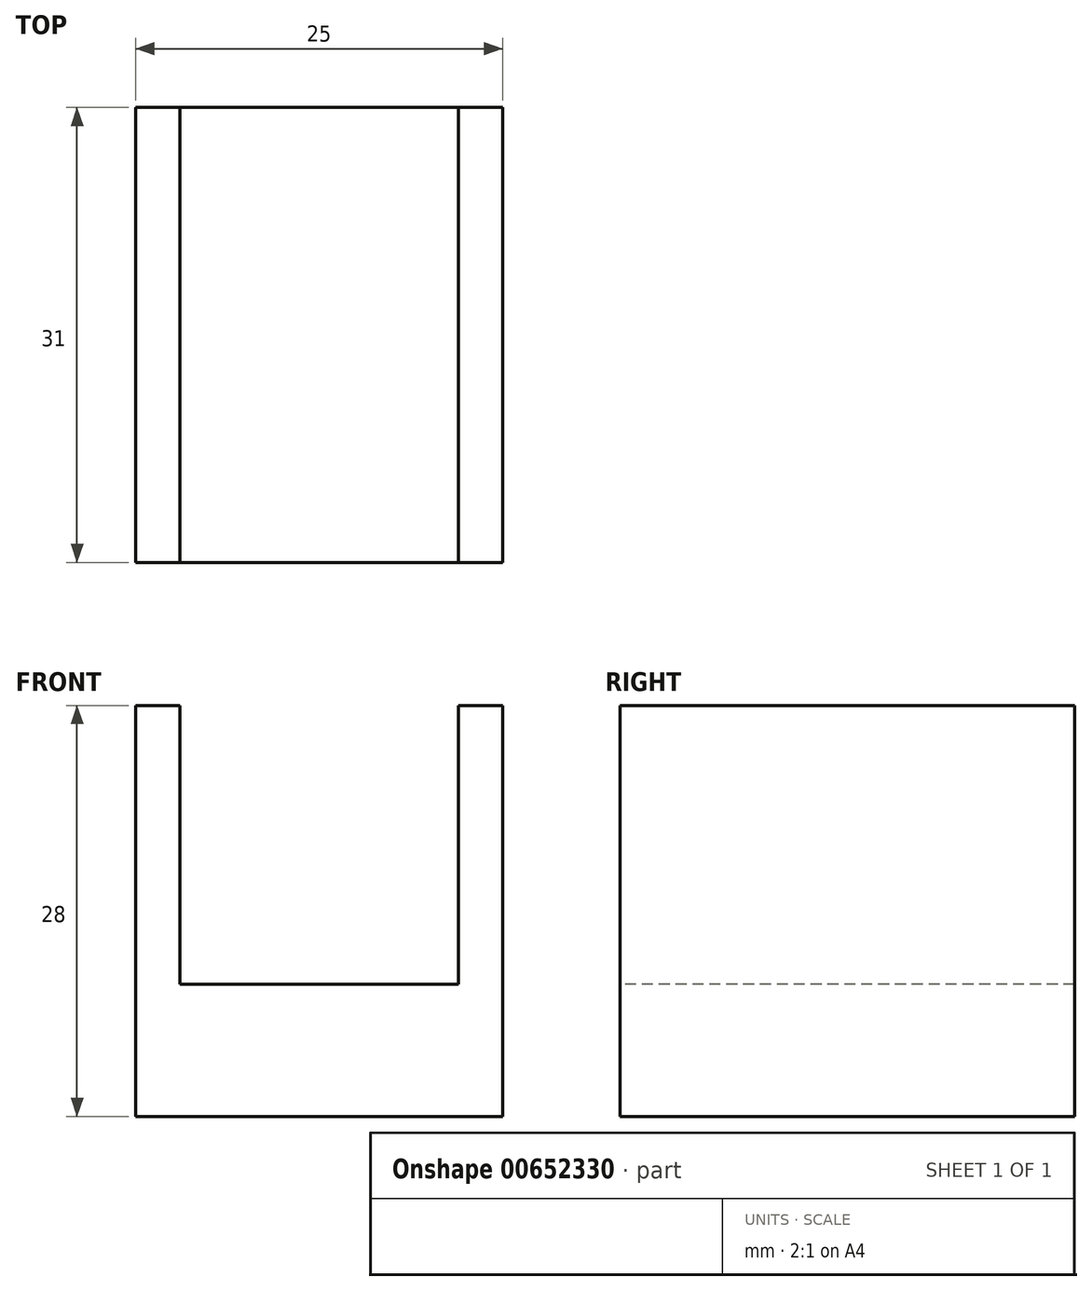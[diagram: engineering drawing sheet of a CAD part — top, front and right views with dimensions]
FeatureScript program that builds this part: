
annotation { "Feature Type Name" : "Feature", "Feature Type Description" : "" }
export const myFeature = defineFeature(function(context is Context, id is Id, definition is map)
    precondition{}
    {
        {
            var Q0;
            Q0=qCreatedBy(makeId("Top.planeOp"),FACE);
            var sketch = newSketch(context, id + "F0", { "sketchPlane" : qUnion([Q0])});
            skLineSegment(sketch, "E0.bottom", {"start": v(0, 0) * mm, "end": v(25, 0) * mm});
            skLineSegment(sketch, "E0.top", {"start": v(0, 31) * mm, "end": v(25, 31) * mm});
            skLineSegment(sketch, "E0.left", {"start": v(0, 0) * mm, "end": v(0, 31) * mm});
            skLineSegment(sketch, "E0.right", {"start": v(25, 0) * mm, "end": v(25, 31) * mm});
            skSolve(sketch);
        }
        {
            var Q0;
            Q0=makeQuery(id+"F0.imprint","IMPRINT",FACE,{"disambiguationData":[TD([[makeQuery(id+"F0.imprint","IMPRINT",EDGE,{"derivedFrom":sQuery(id+"F0.wireOp",EDGE,"E0.bottom")}),1.0]])]});
            extrude(context, id + "F1", {"entities" : qUnion([Q0]), "depth" : 28 * mm, "offsetDistance" : 25 * mm});
        }
        {
            var Q0;
            Q0=makeQuery(id+"F1.opExtrude","SWEPT_FACE",FACE,{"disambiguationData":[OSD([sQuery(id+"F0.wireOp",EDGE,"E0.bottom")])]});
            var sketch = newSketch(context, id + "F2", { "sketchPlane" : qUnion([Q0])});
            skSolve(sketch);
        }
        {
            var Q0;
            {var subQ0=sQuery(id+"F0.wireOp",EDGE,"E0.bottom");var subQ1=makeQuery(id+"F1.opExtrude","CAP_EDGE",EDGE,{"disambiguationData":[OSD([subQ0])],"isStart":true});Q0=makeQuery(id+"F2.imprint","IMPRINT",FACE,{"disambiguationData":[TD([[makeQuery(id+"F2.imprint","IMPRINT",EDGE,{"derivedFrom":subQ1}),1.0]])]});}
            var sketch = newSketch(context, id + "F3", { "sketchPlane" : qUnion([Q0])});
            skLineSegment(sketch, "E1.bottom", {"start": v(3, 28) * mm, "end": v(22, 28) * mm});
            skLineSegment(sketch, "E1.top", {"start": v(3, 9) * mm, "end": v(22, 9) * mm});
            skLineSegment(sketch, "E1.left", {"start": v(3, 28) * mm, "end": v(3, 9) * mm});
            skLineSegment(sketch, "E1.right", {"start": v(22, 28) * mm, "end": v(22, 9) * mm});
            skSolve(sketch);
        }
        {
            var Q0;
            Q0=qSketchRegion(id+"F3",true);
            extrude(context, id + "F4", {"entities" : qUnion([Q0]), "operationType" : NewBodyOperationType.REMOVE, "endBound" : BoundingType.THROUGH_ALL, "oppositeDirection" : true, "depth" : 25 * mm, "offsetDistance" : 25 * mm});
        }
    });
